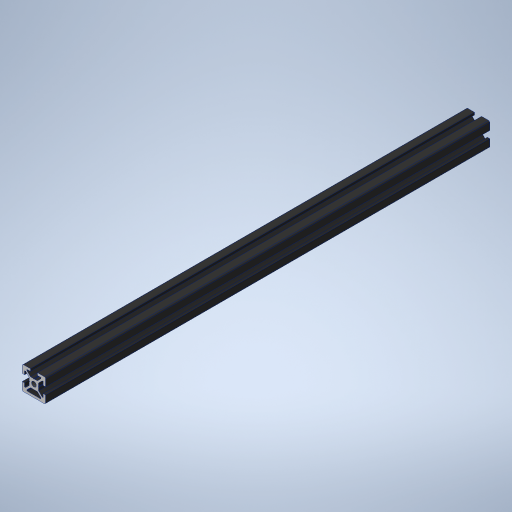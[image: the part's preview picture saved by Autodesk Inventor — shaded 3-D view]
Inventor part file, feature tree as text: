
AUTODESK INVENTOR PART (.ipt)
format: ipt  version: 2024 (Build 280153000, 153)  size: 368,640 bytes
history: native  units: mm
features: other x7, thread x2, sketch x2, extrude x1, hole x1
ambient origin geometry x8: Origin, YZ Plane, XZ Plane, XY Plane, X Axis, Y Axis, Z Axis, Center Point
bodies: Solid1 (feature_tree)
feature tree (13):
  extrude  "Extrusion1"  TaperAngle=0.0deg  [1 undecoded]
  hole  "Hole1"  [1 undecoded]
  other  "C1_XY"
  other  "C1_YZ"
  other  "C1_ZX"
  other  "C1_X"
  other  "C1_Y"
  other  "C1_Z"
  other  "C1_Center"
  thread  "Thread1"  [1 undecoded]
  thread  "Thread2"  [1 undecoded]
  sketch  "Sketch_63"  dims[d2=4.2mm d3=6.0mm d4=4.0mm d5=2.0mm d6=90.0deg d7=440.0mm d8=0.0mm d9=0.0mm d10=10.0mm d11=0.0mm d12=10.0mm d13=0.0mm]
  sketch  "Sketch2"  dims[d0=380.0mm d1=0.0mm]
note: 4 required parameter values undecoded (feature->parameter linkage not recoverable at this tier; creation-order binding heuristic only, values carry confidence <= 0.55)
